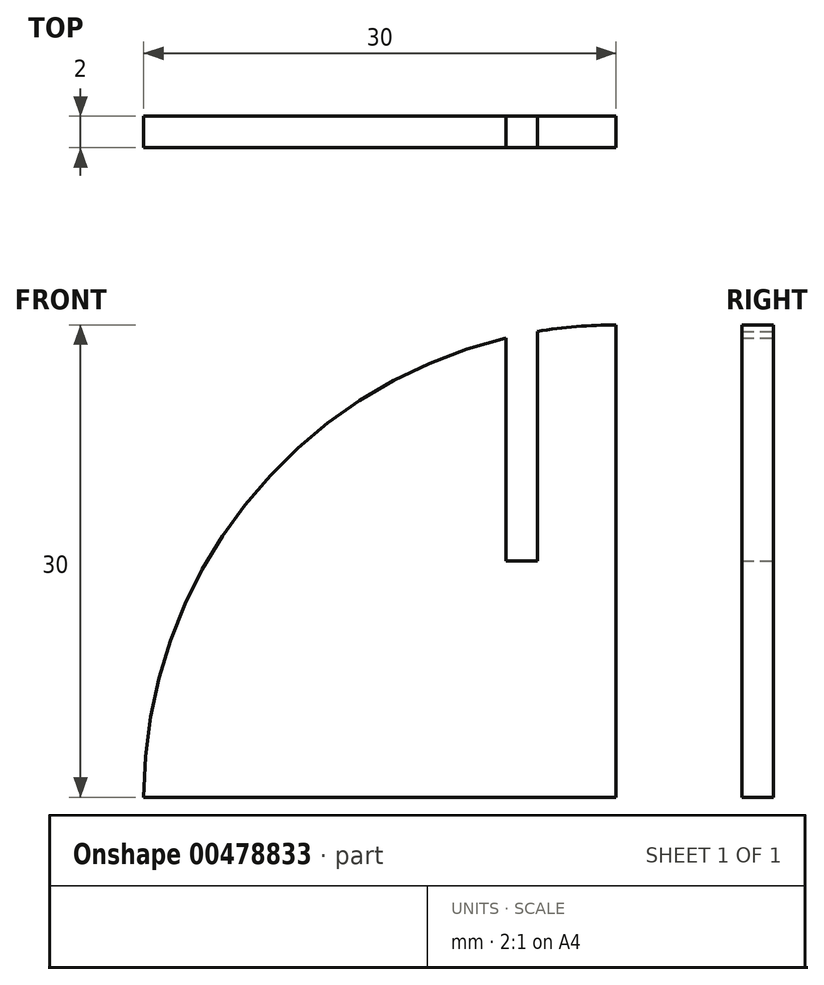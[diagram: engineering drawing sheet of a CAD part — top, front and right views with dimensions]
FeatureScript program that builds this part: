
annotation { "Feature Type Name" : "Feature", "Feature Type Description" : "" }
export const myFeature = defineFeature(function(context is Context, id is Id, definition is map)
    precondition{}
    {
        {
            var Q0;
            Q0=qCreatedBy(makeId("Front.planeOp"),FACE);
            var sketch = newSketch(context, id + "F0", { "sketchPlane" : qUnion([Q0])});
            skArc(sketch, "E0", {"start": v(-30, 0) * mm, "mid": v(-21.21, 21.21) * mm, "end": v(0, 30) * mm});
            skLineSegment(sketch, "E1", {"start": v(0, 30) * mm, "end": v(0, 0) * mm});
            skLineSegment(sketch, "E2", {"start": v(-30, 0) * mm, "end": v(0, 0) * mm});
            skSolve(sketch);
        }
        {
            var Q0;
            Q0 = qSketchRegion(id + "F0", true);
            extrude(context, id + "F1", {"entities" : qUnion([Q0]), "depth" : 2 * mm});
        }
        {
            var Q0;
            Q0=qCreatedBy(makeId("Front.planeOp"),FACE);
            var sketch = newSketch(context, id + "F2", { "sketchPlane" : qUnion([Q0])});
            skLineSegment(sketch, "E3.bottom", {"start": v(-7, 29.96) * mm, "end": v(-5, 29.96) * mm});
            skLineSegment(sketch, "E3.top", {"start": v(-7, 15) * mm, "end": v(-5, 15) * mm});
            skLineSegment(sketch, "E3.left", {"start": v(-7, 29.96) * mm, "end": v(-7, 15) * mm});
            skLineSegment(sketch, "E3.right", {"start": v(-5, 29.96) * mm, "end": v(-5, 15) * mm});
            skSolve(sketch);
        }
        {
            var Q0;
            Q0 = qSketchRegion(id + "F2", true);
            extrude(context, id + "F3", {"entities" : qUnion([Q0]), "operationType" : NewBodyOperationType.REMOVE, "depth" : 25 * mm});
        }
    });
